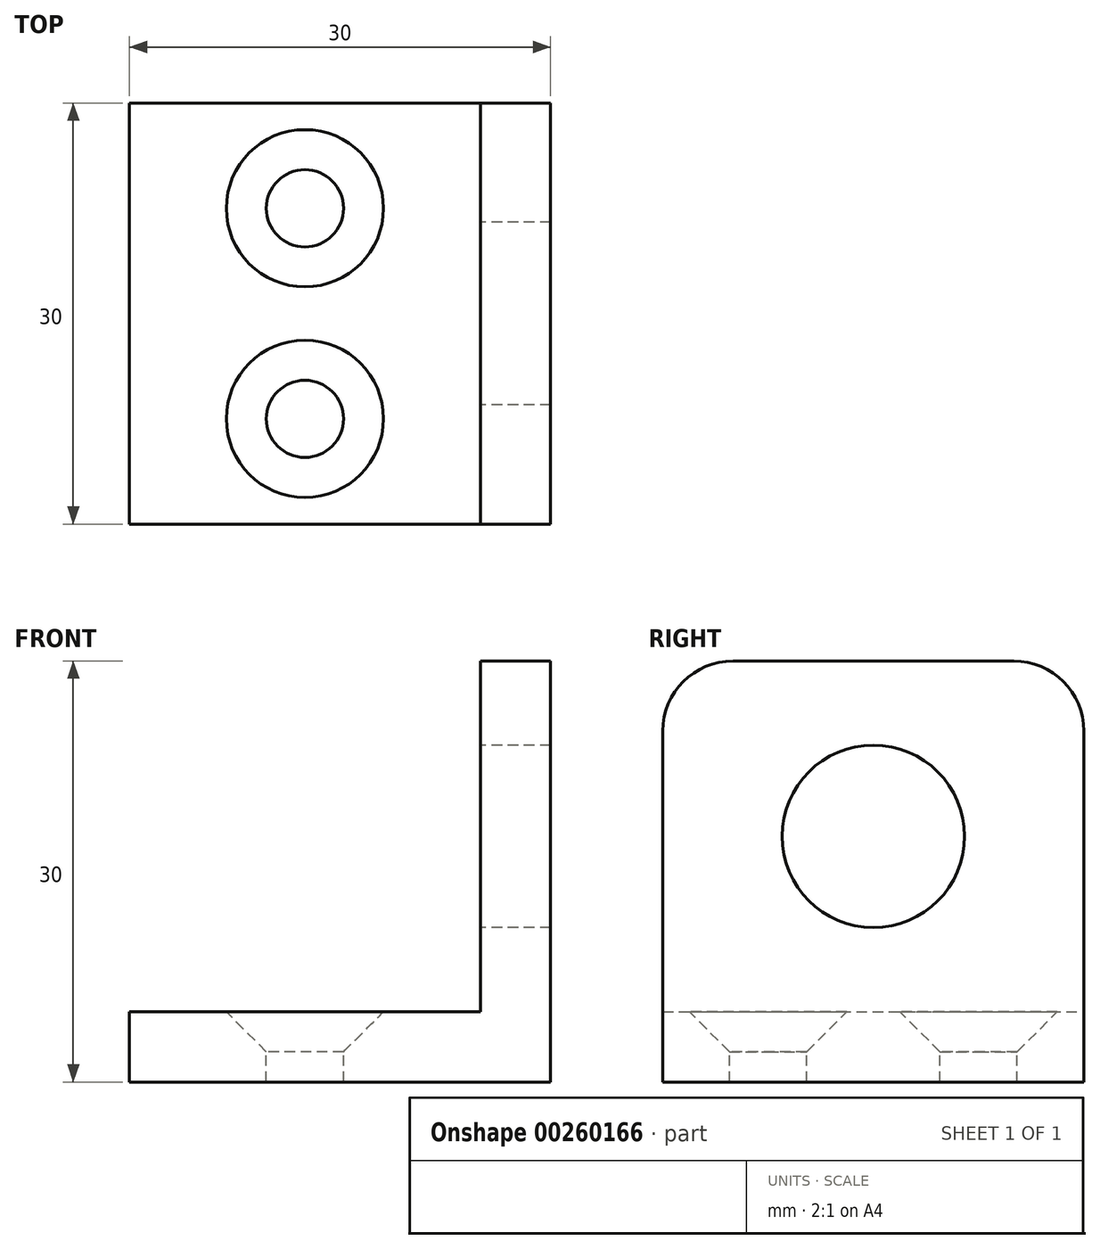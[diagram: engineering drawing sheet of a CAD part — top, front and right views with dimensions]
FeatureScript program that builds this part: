
annotation { "Feature Type Name" : "Feature", "Feature Type Description" : "" }
export const myFeature = defineFeature(function(context is Context, id is Id, definition is map)
    precondition{}
    {
        {
            var Q0;
            Q0=qCreatedBy(makeId("Front.planeOp"),FACE);
            var sketch = newSketch(context, id + "F0", { "sketchPlane" : qUnion([Q0])});
            skLineSegment(sketch, "E0.bottom", {"start": v(15, -2.5) * mm, "end": v(-15, -2.5) * mm});
            skLineSegment(sketch, "E0.top", {"start": v(10, 2.5) * mm, "end": v(-15, 2.5) * mm});
            skLineSegment(sketch, "E0.left", {"start": v(15, -2.5) * mm, "end": v(15, 2.5) * mm});
            skLineSegment(sketch, "E0.right", {"start": v(-15, -2.5) * mm, "end": v(-15, 2.5) * mm});
            skPoint(sketch, "E0.middle", {"position": v(0, 0) * mm});
            skLineSegment(sketch, "E1.top", {"start": v(15, 27.5) * mm, "end": v(10, 27.5) * mm});
            skLineSegment(sketch, "E1.left", {"start": v(15, -2.5) * mm, "end": v(15, 27.5) * mm});
            skLineSegment(sketch, "E1.right", {"start": v(10, 2.5) * mm, "end": v(10, 27.5) * mm});
            skSolve(sketch);
        }
        {
            var Q0;
            {var subQ1=sQuery(id+"F0.wireOp",EDGE,"E0.bottom");Q0=makeQuery(id+"F0.imprint","IMPRINT",FACE,{"disambiguationData":[TD([[makeQuery(id+"F0.imprint","IMPRINT",EDGE,{"derivedFrom":subQ1}),-1.0]])]});}
            extrude(context, id + "F1", {"entities" : qUnion([Q0]), "depth" : 30 * mm});
        }
        {
            var Q0;
            Q0=makeQuery(id+"F1.opExtrude","CAP_EDGE",EDGE,{"disambiguationData":[OSD([sQuery(id+"F0.wireOp",EDGE,"E1.top")])],"isStart":true});
            var Q1;
            Q1=makeQuery(id+"F1.opExtrude","CAP_EDGE",EDGE,{"disambiguationData":[OSD([sQuery(id+"F0.wireOp",EDGE,"E1.top")])],"isStart":false});
            fillet(context, id + "F2", {"entities" : qUnion([Q0, Q1]), "radius" : 5 * mm, "tangentPropagation" : true, "allowEdgeOverflow" : false});
        }
        {
            var Q0;
            Q0=makeQuery(id+"F1.opExtrude","SWEPT_FACE",FACE,{"disambiguationData":[OSD([sQuery(id+"F0.wireOp",EDGE,"E1.right")])]});
            var sketch = newSketch(context, id + "F3", { "sketchPlane" : qUnion([Q0])});
            skCircle(sketch, "E2", {"center": v(15, 15) * mm, "radius": 6.5 * mm});
            skPoint(sketch, "E2.centerSnap0", {"position": v(15, 27.5) * mm});
            skSolve(sketch);
        }
        {
            var Q0;
            Q0=makeQuery(id+"F3.imprint","IMPRINT",FACE,{"disambiguationData":[TD([[makeQuery(id+"F3.imprint","IMPRINT",EDGE,{"derivedFrom":sQuery(id+"F3.wireOp",EDGE,"E2")}),1.0]])]});
            extrude(context, id + "F4", {"entities" : qUnion([Q0]), "operationType" : NewBodyOperationType.REMOVE, "endBound" : BoundingType.THROUGH_ALL, "oppositeDirection" : true, "depth" : 25 * mm});
        }
        {
            var Q0;
            Q0=makeQuery(id+"F1.opExtrude","SWEPT_FACE",FACE,{"disambiguationData":[OSD([sQuery(id+"F0.wireOp",EDGE,"E0.top")])]});
            var sketch = newSketch(context, id + "F5", { "sketchPlane" : qUnion([Q0])});
            skPoint(sketch, "E3", {"position": v(-2.5, -22.5) * mm});
            skPoint(sketch, "E4", {"position": v(-2.5, -7.5) * mm});
            skSolve(sketch);
        }
        {
            var Q0;
            Q0=sQuery(id+"F5.wireOp",VERTEX,"E3");
            var Q1;
            Q1=sQuery(id+"F5.wireOp",VERTEX,"E4");
            var Q2;
            Q2=makeQuery(id+"F1.opExtrude","SWEPT_BODY",BODY,{"disambiguationData":[OSD([sQuery(id+"F0.wireOp",EDGE,"E0.bottom"),sQuery(id+"F0.wireOp",EDGE,"E0.top"),sQuery(id+"F0.wireOp",EDGE,"E0.right"),sQuery(id+"F0.wireOp",EDGE,"E1.top"),sQuery(id+"F0.wireOp",EDGE,"E1.left"),sQuery(id+"F0.wireOp",EDGE,"E1.right")])]});
            hole(context, id + "F6", {"style" : HoleStyle.C_SINK, "endStyle" : HoleEndStyle.BLIND, "standardTappedOrClearance" : lookupTablePath({ "standard" : "ISO", "fit" : "Normal", "size" : "M5", "type" : "Clearance" }), "standardBlindInLast" : lookupTablePath({ "fit" : "Standard", "standard" : "ISO", "size" : "M5", "type" : "Clearance" }), "holeDiameter" : 5.5 * mm, "cSinkDiameter" : 11.2 * mm, "cSinkAngle" : 90 * degree, "holeDepth" : 18 * mm, "tappedDepth" : 32 * mm, "tapClearance" : 3, "startFromSketch" : true, "locations" : qUnion([Q0, Q1]), "scope" : qUnion([Q2])});
        }
    });
